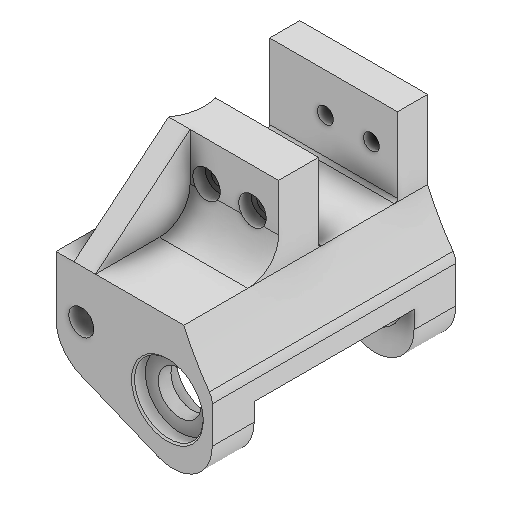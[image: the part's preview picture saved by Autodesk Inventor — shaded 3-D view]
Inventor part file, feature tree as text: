
AUTODESK INVENTOR PART (.ipt)
format: ipt  version: 2025 (Build 290162000, 162)  size: 475,136 bytes
history: native  units: in
note: dims shown in document units (in); Inventor stores cm internally (conversion verified against a paired STEP export)
features: extrude x19, sketch x19, projected_geometry x13, fillet x9, mirror x3, reference x3, other x3, chamfer x2, thicken_offset x1, plane x1
ambient origin geometry x8: Origin, YZ Plane, XZ Plane, XY Plane, X Axis, Y Axis, Z Axis, Center Point
bodies: Solid1 (feature_tree)
feature tree (73):
  extrude  "Extrusion1"  Depth=0.25in
  extrude  "Extrusion2"  Depth=2.0in
  extrude  "Extrusion7"  Depth=0.8809in
  extrude  "Extrusion10"  Depth=0.2165in TaperAngle=0.0deg
  extrude  "Extrusion11"  Depth=0.315in
  extrude  "Extrusion12"  TaperAngle=0.0deg  [1 undecoded]
  extrude  "Extrusion13"  Depth=0.3937in TaperAngle=0.0deg
  mirror  "Mirror1"
  fillet  "Fillet5"  Radius=0.3937in
  extrude  "Extrusion14"  Depth=0.3937in
  fillet  "Fillet6"  [1 undecoded]
  extrude  "Extrusion15"  Depth=0.3937in
  thicken_offset  "Thicken1"
  fillet  "Fillet7"  Radius=0.3858in
  extrude  "Extrusion16"  Depth=0.5118in
  extrude  "Extrusion17"  Depth=0.1969in
  fillet  "Fillet8"  Radius=1.0in
  extrude  "Extrusion18"  Depth=0.3937in
  extrude  "Extrusion19"  Depth=1.0in TaperAngle=0.0deg
  extrude  "Extrusion20"  Depth=0.315in
  extrude  "Extrusion21"  Depth=0.3228in
  extrude  "Extrusion22"  Depth=0.2756in
  extrude  "Extrusion23"  Depth=0.2047in
  plane  "Work Plane1"
  mirror  "Mirror2"
  fillet  "Fillet9"  Radius=0.2047in
  fillet  "Fillet10"  [1 undecoded]
  fillet  "Fillet11"  Radius=0.3543in
  extrude  "Extrusion24"  Depth=0.315in TaperAngle=0.0deg
  extrude  "Extrusion25"  Depth=0.5in
  fillet  "Fillet12"  Radius=0.0394in
  fillet  "Fillet13"  Radius=0.1969in
  chamfer  "Chamfer1"  [1 undecoded]
  chamfer  "Chamfer2"  Distance=0.5in
  mirror  "Mirror3"
  sketch  "Sketch1"  dims[d1=1.005in d2=0.25in]
  sketch  "Sketch2"  dims[d3=2.0in d4=0.0in d5=0.5512in]
  projected_geometry  "Projected Loop1"
  sketch  "Sketch7"  dims[d6=0.0in d7=0.0in d21=0.8809in]
  sketch  "Sketch10"  dims[d22=0.1575in d23=0.0in d32=0.2165in d33=0.0in]
  projected_geometry  "Projected Loop7"
  sketch  "Sketch11"  dims[d34=1.1024in d35=0.315in]
  sketch  "Sketch12"  dims[d36=0.2047in d37=0.0in d38=0.0in]
  projected_geometry  "Projected Loop8"
  sketch  "Sketch13"  dims[d39=0.3937in d40=0.0in d42=1.0236in d43=0.0in d45=0.3937in]
  projected_geometry  "Projected Loop9"
  sketch  "Sketch14"  dims[d46=1.0236in d47=0.0in d48=0.3937in d49=0.0in d50=0.0in]
  projected_geometry  "Projected Loop10"
  sketch  "Sketch15"  dims[d51=0.0591in d52=0.1in d53=0.3937in d54=0.3858in]
  projected_geometry  "Projected Loop11"
  sketch  "Sketch16"  dims[d55=0.0079in d56=0.5118in]
  projected_geometry  "Projected Loop12"
  reference  "Reference1"
  sketch  "Sketch17"  dims[d57=0.2756in d58=0.1969in d59=1.0in d60=0.0in]
  projected_geometry  "Projected Loop13"
  sketch  "Sketch18"  dims[d61=1.0in d62=0.0in d63=0.3937in]
  projected_geometry  "Projected Loop14"
  reference  "Reference2"
  sketch  "Sketch19"  dims[d64=0.2047in d65=1.0in d66=0.0in]
  sketch  "Sketch20"  dims[d67=0.315in d68=0.315in]
  sketch  "Sketch21"  dims[d69=0.1969in d70=0.0in d71=0.3228in]
  sketch  "Sketch22"  dims[d72=0.315in d73=0.0in d74=0.2756in]
  reference  "Reference3"
  sketch  "Sketch23"  dims[d75=0.4724in d76=0.0in d77=0.2047in d78=0.2047in d79=0.0in d80=0.0in d81=0.3543in]
  projected_geometry  "Projected Loop15"
  sketch  "Sketch24"  dims[d82=0.3543in d83=0.315in d84=0.0in]
  projected_geometry  "Projected Loop16"
  projected_geometry  "Projected Loop17"
  sketch  "Sketch25"  dims[d85=0.7874in d86=0.1969in d87=0.0394in d88=0.1969in d89=0.0in d90=0.0in d91=0.0in d92=0.5in d93=0.5in d94=0.0197in d95=0.0787in d96=45.0deg d97=0.1181in d98=0.0787in d99=45.0deg d24=0.0344in d27=0.0in d28=0.0in d29=0.0in d30=0.0in]
  projected_geometry  "Projected Loop18"
  other  "<userpath>\Desktop\puppycat\singleSwingarmV2.iam"
  other  "singleSwingarmV2.iam"
  other  "trackBase:1"
note: 4 required parameter values undecoded (feature->parameter linkage not recoverable at this tier; creation-order binding heuristic only, values carry confidence <= 0.55)
